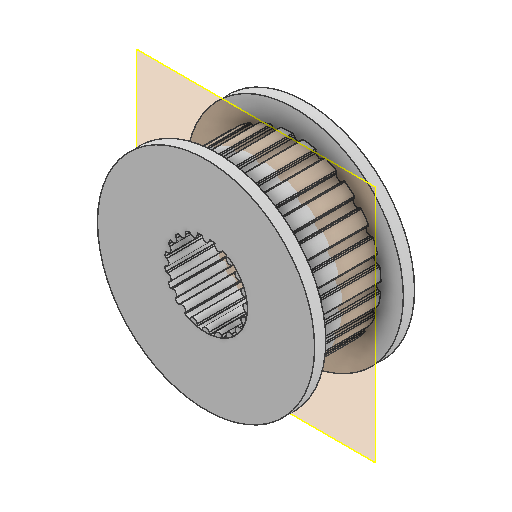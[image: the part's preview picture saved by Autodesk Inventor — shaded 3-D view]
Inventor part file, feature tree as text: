
AUTODESK INVENTOR PART (.ipt)
format: ipt  version: 2025.2 (Build 292293000, 293)  size: 798,208 bytes
history: native  units: in
note: dims shown in document units (in); Inventor stores cm internally (conversion verified against a paired STEP export)
features: sketch x6, extrude x4, plane x1
ambient origin geometry x8: Origin, YZ Plane, XZ Plane, XY Plane, X Axis, Y Axis, Z Axis, Center Point
bodies: Solid1 (feature_tree)
feature tree (11):
  extrude  "Extrusion1"  Depth=1.2402in
  plane  "Work Plane1"
  extrude  "Extrusion2"  [1 undecoded]
  extrude  "Extrusion3"  Depth=0.4429in TaperAngle=0.0deg
  extrude  "Extrusion4"  TaperAngle=0.0deg  [1 undecoded]
  sketch  "Sketch1"  dims[d0=0.4724in d1=1.2402in]
  sketch  "Sketch2"  dims[d5=0.9843in d6=0.4429in d7=0.0in]
  sketch  "Sketch3"  dims[d12=0.5709in d13=0.0in]
  sketch  "Sketch Circular Pattern1"  dims[d2=0.5709in d3=0.0in d4=-0.2854in]
  sketch  "Sketch5"  dims[d18=14.5669in d20=360.0deg d24=0.0in d26=0.0in d27=0.0in d28=0.0in d29=0.0in d30=9.4488in d32=360.0deg d34=0.4429in d35=0.0in]
  sketch  "Sketch Circular Pattern2"  dims[d8=0.0in d9=0.0in]
note: 2 required parameter values undecoded (feature->parameter linkage not recoverable at this tier; creation-order binding heuristic only, values carry confidence <= 0.55)
